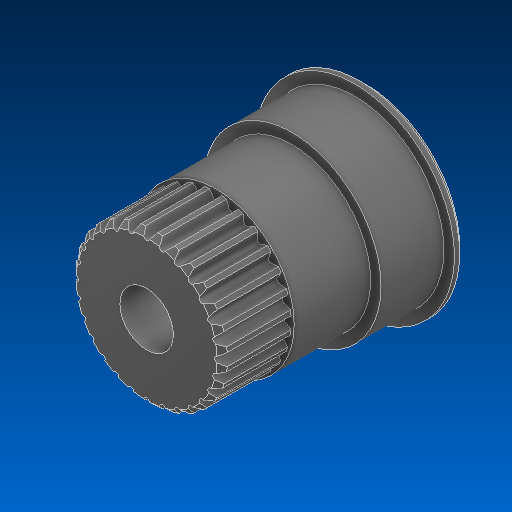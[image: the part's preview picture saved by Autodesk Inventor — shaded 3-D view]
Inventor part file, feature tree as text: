
AUTODESK INVENTOR PART (.ipt)
format: ipt  version: 2022.2 (Build 262287000, 287)  size: 600,576 bytes
history: native  units: in
note: dims shown in document units (in); Inventor stores cm internally (conversion verified against a paired STEP export)
features: chamfer x1
ambient origin geometry x8: Origin, YZ Plane, XZ Plane, XY Plane, X Axis, Y Axis, Z Axis, Center Point
bodies: Solid1 (feature_tree)
feature tree (1):
  chamfer  "Chamfer1"  [1 undecoded]
note: 1 required parameter value undecoded (feature->parameter linkage not recoverable at this tier; creation-order binding heuristic only, values carry confidence <= 0.55)
